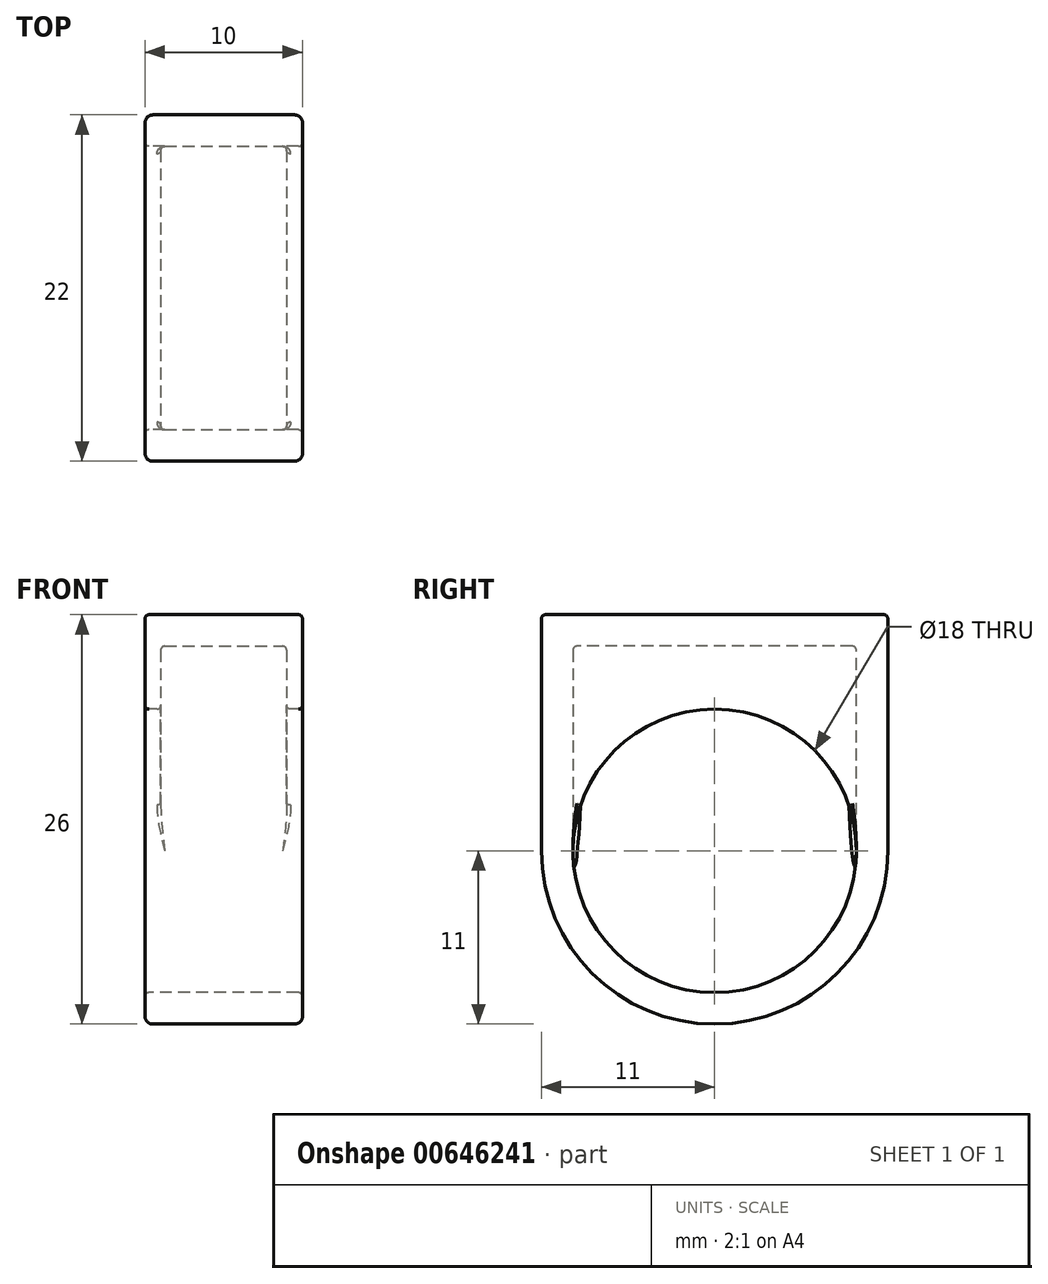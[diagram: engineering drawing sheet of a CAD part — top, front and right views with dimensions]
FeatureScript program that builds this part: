
annotation { "Feature Type Name" : "Feature", "Feature Type Description" : "" }
export const myFeature = defineFeature(function(context is Context, id is Id, definition is map)
    precondition{}
    {
        {
            var Q0;
            Q0=qCreatedBy(makeId("Right.planeOp"),FACE);
            var sketch = newSketch(context, id + "F0", { "sketchPlane" : qUnion([Q0])});
            skCircle(sketch, "E0", {"center": v(0, 0) * mm, "radius": 9 * mm});
            skCircle(sketch, "E1", {"center": v(0, 0) * mm, "radius": 11 * mm});
            skLineSegment(sketch, "E2", {"start": v(11, 0) * mm, "end": v(11, 15) * mm});
            skLineSegment(sketch, "E3", {"start": v(-11, 0) * mm, "end": v(-11, 15) * mm});
            skLineSegment(sketch, "E4", {"start": v(-11, 15) * mm, "end": v(11, 15) * mm});
            skSolve(sketch);
        }
        {
            var Q0;
            Q0=makeQuery(id+"F0.imprint","IMPRINT",FACE,{"disambiguationData":[TD([[makeQuery(id+"F0.imprint","IMPRINT",EDGE,{"derivedFrom":sQuery(id+"F0.wireOp",EDGE,"E0")}),-1.0]])]});
            var Q1;
            {var subQ0=sQuery(id+"F0.wireOp",EDGE,"E2");Q1=makeQuery(id+"F0.imprint","IMPRINT",FACE,{"disambiguationData":[TD([[makeQuery(id+"F0.imprint","IMPRINT",EDGE,{"derivedFrom":subQ0}),1.0]])]});}
            extrude(context, id + "F1", {"entities" : qUnion([Q0, Q1]), "endBound" : BoundingType.SYMMETRIC, "depth" : 10 * mm, "offsetDistance" : 25 * mm});
        }
        {
            var Q0;
            Q0=qCreatedBy(makeId("Right.planeOp"),FACE);
            var sketch = newSketch(context, id + "F2", { "sketchPlane" : qUnion([Q0])});
            skArc(sketch, "E5.0", {"start": v(-9, 0) * mm, "mid": v(0, -9) * mm, "end": v(9, 0) * mm});
            skLineSegment(sketch, "E5.1", {"start": v(-9, 13) * mm, "end": v(-9, 0) * mm});
            skLineSegment(sketch, "E5.2", {"start": v(9, 13) * mm, "end": v(-9, 13) * mm});
            skLineSegment(sketch, "E5.3", {"start": v(9, 0) * mm, "end": v(9, 13) * mm});
            skSolve(sketch);
        }
        {
            var Q0;
            Q0 = qSketchRegion(id + "F2", true);
            extrude(context, id + "F3", {"entities" : qUnion([Q0]), "operationType" : NewBodyOperationType.REMOVE, "endBound" : BoundingType.SYMMETRIC, "oppositeDirection" : true, "depth" : 8 * mm, "offsetDistance" : 25 * mm});
        }
        {
            var Q0;
            Q0=makeQuery(id+"F1.opExtrude","CAP_EDGE",EDGE,{"disambiguationData":[OSD([sQuery(id+"F0.wireOp",EDGE,"E3")])],"isStart":false});
            var Q1;
            Q1=makeQuery(id+"F1.opExtrude","CAP_EDGE",EDGE,{"disambiguationData":[OSD([sQuery(id+"F0.wireOp",EDGE,"E3")])],"isStart":true});
            fillet(context, id + "F4", {"entities" : qUnion([Q0, Q1]), "radius" : 0.5 * mm, "tangentPropagation" : true, "allowEdgeOverflow" : false});
        }
        {
            var Q0;
            Q0=makeQuery(id+"F1.opExtrude","CAP_EDGE",EDGE,{"disambiguationData":[OSD([sQuery(id+"F0.wireOp",EDGE,"E0")])],"isStart":false});
            var Q1;
            Q1=makeQuery(id+"F1.opExtrude","CAP_EDGE",EDGE,{"disambiguationData":[OSD([sQuery(id+"F0.wireOp",EDGE,"E0")])],"isStart":true});
            var Q2;
            Q2=makeQuery(id+"F1.opExtrude","SWEPT_EDGE",EDGE,{"disambiguationData":[OSD([sQuery(id+"F0.wireOp",EDGE,"E3"),sQuery(id+"F0.wireOp",EDGE,"E4")])]});
            var Q3;
            Q3=makeQuery(id+"F3.boolean.opBoolean","COPY",EDGE,{"derivedFrom":makeQuery(id+"F3.opExtrude","SWEPT_EDGE",EDGE,{"disambiguationData":[OSD([sQuery(id+"F2.wireOp",EDGE,"E5.0"),sQuery(id+"F2.wireOp",EDGE,"E5.3")])]})});
            var Q4;
            Q4=makeQuery(id+"F3.boolean.opBoolean","INTERSECT",EDGE,{"derivedFrom":[makeQuery(id+"F1.opExtrude","SWEPT_FACE",FACE,{"disambiguationData":[OSD([sQuery(id+"F0.wireOp",EDGE,"E0")])]}),makeQuery(id+"F3.opExtrude","CAP_FACE",FACE,{"disambiguationData":[OSD([sQuery(id+"F2.wireOp",EDGE,"E5.0"),sQuery(id+"F2.wireOp",EDGE,"E5.1"),sQuery(id+"F2.wireOp",EDGE,"E5.2"),sQuery(id+"F2.wireOp",EDGE,"E5.3")])],"isStart":true})]});
            var Q5;
            {var subQ0=sQuery(id+"F0.wireOp",EDGE,"E1");Q5=makeQuery(id+"F4.opFillet","BLEND_EDGE",EDGE,{"blendedFrom":[makeQuery(id+"F1.opExtrude","CAP_EDGE",EDGE,{"disambiguationData":[OSD([subQ0])],"isStart":true}),makeQuery(id+"F1.opExtrude","SWEPT_FACE",FACE,{"disambiguationData":[OSD([subQ0])]})],"blendedInto":[makeQuery(id+"F1.opExtrude","SWEPT_FACE",FACE,{"disambiguationData":[OSD([subQ0])]})]});}
            var Q6;
            Q6=makeQuery(id+"F4.opFillet","BLEND_EDGE",EDGE,{"blendedFrom":[makeQuery(id+"F1.opExtrude","CAP_EDGE",EDGE,{"disambiguationData":[OSD([sQuery(id+"F0.wireOp",EDGE,"E1")])],"isStart":false}),makeQuery(id+"F1.opExtrude","CAP_EDGE",EDGE,{"disambiguationData":[OSD([sQuery(id+"F0.wireOp",EDGE,"E3")])],"isStart":false})],"blendedInto":[]});
            var Q7;
            {var subQ0=sQuery(id+"F0.wireOp",EDGE,"E1");Q7=makeQuery(id+"F4.opFillet","BLEND_EDGE",EDGE,{"blendedFrom":[makeQuery(id+"F1.opExtrude","CAP_EDGE",EDGE,{"disambiguationData":[OSD([subQ0])],"isStart":false}),makeQuery(id+"F1.opExtrude","CAP_FACE",FACE,{"disambiguationData":[OSD([sQuery(id+"F0.wireOp",EDGE,"E0"),subQ0,sQuery(id+"F0.wireOp",EDGE,"E2"),sQuery(id+"F0.wireOp",EDGE,"E3"),sQuery(id+"F0.wireOp",EDGE,"E4")])],"isStart":false})],"blendedInto":[makeQuery(id+"F1.opExtrude","CAP_FACE",FACE,{"disambiguationData":[OSD([sQuery(id+"F0.wireOp",EDGE,"E0"),subQ0,sQuery(id+"F0.wireOp",EDGE,"E2"),sQuery(id+"F0.wireOp",EDGE,"E3"),sQuery(id+"F0.wireOp",EDGE,"E4")])],"isStart":false})]});}
            var Q8;
            {var subQ0=sQuery(id+"F0.wireOp",EDGE,"E1");Q8=makeQuery(id+"F4.opFillet","BLEND_EDGE",EDGE,{"blendedFrom":[makeQuery(id+"F1.opExtrude","CAP_EDGE",EDGE,{"disambiguationData":[OSD([subQ0])],"isStart":false}),makeQuery(id+"F1.opExtrude","SWEPT_FACE",FACE,{"disambiguationData":[OSD([subQ0])]})],"blendedInto":[makeQuery(id+"F1.opExtrude","SWEPT_FACE",FACE,{"disambiguationData":[OSD([subQ0])]})]});}
            var Q9;
            Q9=makeQuery(id+"F1.opExtrude","CAP_EDGE",EDGE,{"disambiguationData":[OSD([sQuery(id+"F0.wireOp",EDGE,"E4")])],"isStart":true});
            var Q10;
            Q10=makeQuery(id+"F1.opExtrude","CAP_EDGE",EDGE,{"disambiguationData":[OSD([sQuery(id+"F0.wireOp",EDGE,"E4")])],"isStart":false});
            var Q11;
            Q11=makeQuery(id+"F1.opExtrude","SWEPT_EDGE",EDGE,{"disambiguationData":[OSD([sQuery(id+"F0.wireOp",EDGE,"E1"),sQuery(id+"F0.wireOp",EDGE,"E2")])]});
            var Q12;
            {var subQ0=sQuery(id+"F0.wireOp",EDGE,"E2");Q12=makeQuery(id+"F4.opFillet","BLEND_EDGE",EDGE,{"blendedFrom":[makeQuery(id+"F1.opExtrude","CAP_EDGE",EDGE,{"disambiguationData":[OSD([subQ0])],"isStart":true}),makeQuery(id+"F1.opExtrude","SWEPT_FACE",FACE,{"disambiguationData":[OSD([subQ0])]})],"blendedInto":[makeQuery(id+"F1.opExtrude","SWEPT_FACE",FACE,{"disambiguationData":[OSD([subQ0])]})]});}
            var Q13;
            Q13=makeQuery(id+"F4.opFillet","BLEND_EDGE",EDGE,{"blendedFrom":[makeQuery(id+"F1.opExtrude","CAP_EDGE",EDGE,{"disambiguationData":[OSD([sQuery(id+"F0.wireOp",EDGE,"E2")])],"isStart":true}),makeQuery(id+"F1.opExtrude","SWEPT_FACE",FACE,{"disambiguationData":[OSD([sQuery(id+"F0.wireOp",EDGE,"E4")])]})],"blendedInto":[makeQuery(id+"F1.opExtrude","SWEPT_FACE",FACE,{"disambiguationData":[OSD([sQuery(id+"F0.wireOp",EDGE,"E4")])]})]});
            var Q14;
            {var subQ0=sQuery(id+"F0.wireOp",EDGE,"E2");Q14=makeQuery(id+"F4.opFillet","BLEND_EDGE",EDGE,{"blendedFrom":[makeQuery(id+"F1.opExtrude","CAP_EDGE",EDGE,{"disambiguationData":[OSD([subQ0])],"isStart":false}),makeQuery(id+"F1.opExtrude","CAP_FACE",FACE,{"disambiguationData":[OSD([sQuery(id+"F0.wireOp",EDGE,"E0"),sQuery(id+"F0.wireOp",EDGE,"E1"),subQ0,sQuery(id+"F0.wireOp",EDGE,"E3"),sQuery(id+"F0.wireOp",EDGE,"E4")])],"isStart":false})],"blendedInto":[makeQuery(id+"F1.opExtrude","CAP_FACE",FACE,{"disambiguationData":[OSD([sQuery(id+"F0.wireOp",EDGE,"E0"),sQuery(id+"F0.wireOp",EDGE,"E1"),subQ0,sQuery(id+"F0.wireOp",EDGE,"E3"),sQuery(id+"F0.wireOp",EDGE,"E4")])],"isStart":false})]});}
            var Q15;
            Q15=makeQuery(id+"F1.opExtrude","SWEPT_EDGE",EDGE,{"disambiguationData":[OSD([sQuery(id+"F0.wireOp",EDGE,"E2"),sQuery(id+"F0.wireOp",EDGE,"E4")])]});
            var Q16;
            Q16=makeQuery(id+"F1.opExtrude","SWEPT_EDGE",EDGE,{"disambiguationData":[OSD([sQuery(id+"F0.wireOp",EDGE,"E1"),sQuery(id+"F0.wireOp",EDGE,"E3")])]});
            var Q17;
            Q17=makeQuery(id+"F4.opFillet","BLEND_EDGE",EDGE,{"blendedFrom":[makeQuery(id+"F1.opExtrude","CAP_EDGE",EDGE,{"disambiguationData":[OSD([sQuery(id+"F0.wireOp",EDGE,"E1")])],"isStart":true}),makeQuery(id+"F1.opExtrude","CAP_EDGE",EDGE,{"disambiguationData":[OSD([sQuery(id+"F0.wireOp",EDGE,"E3")])],"isStart":true})],"blendedInto":[]});
            var Q18;
            {var subQ0=sQuery(id+"F0.wireOp",EDGE,"E1");Q18=makeQuery(id+"F4.opFillet","BLEND_EDGE",EDGE,{"blendedFrom":[makeQuery(id+"F1.opExtrude","CAP_EDGE",EDGE,{"disambiguationData":[OSD([subQ0])],"isStart":true}),makeQuery(id+"F1.opExtrude","CAP_FACE",FACE,{"disambiguationData":[OSD([sQuery(id+"F0.wireOp",EDGE,"E0"),subQ0,sQuery(id+"F0.wireOp",EDGE,"E2"),sQuery(id+"F0.wireOp",EDGE,"E3"),sQuery(id+"F0.wireOp",EDGE,"E4")])],"isStart":true})],"blendedInto":[makeQuery(id+"F1.opExtrude","CAP_FACE",FACE,{"disambiguationData":[OSD([sQuery(id+"F0.wireOp",EDGE,"E0"),subQ0,sQuery(id+"F0.wireOp",EDGE,"E2"),sQuery(id+"F0.wireOp",EDGE,"E3"),sQuery(id+"F0.wireOp",EDGE,"E4")])],"isStart":true})]});}
            var Q19;
            Q19=makeQuery(id+"F3.boolean.opBoolean","COPY",EDGE,{"derivedFrom":makeQuery(id+"F3.opExtrude","SWEPT_EDGE",EDGE,{"disambiguationData":[OSD([sQuery(id+"F2.wireOp",EDGE,"E5.0"),sQuery(id+"F2.wireOp",EDGE,"E5.1")])]})});
            var Q20;
            Q20=makeQuery(id+"F3.boolean.opBoolean","COPY",EDGE,{"derivedFrom":makeQuery(id+"F3.opExtrude","SWEPT_EDGE",EDGE,{"disambiguationData":[OSD([sQuery(id+"F2.wireOp",EDGE,"E5.1"),sQuery(id+"F2.wireOp",EDGE,"E5.2")])]})});
            var Q21;
            Q21=makeQuery(id+"F3.boolean.opBoolean","COPY",EDGE,{"derivedFrom":makeQuery(id+"F3.opExtrude","SWEPT_EDGE",EDGE,{"disambiguationData":[OSD([sQuery(id+"F2.wireOp",EDGE,"E5.2"),sQuery(id+"F2.wireOp",EDGE,"E5.3")])]})});
            var Q22;
            Q22=makeQuery(id+"F3.boolean.opBoolean","COPY",EDGE,{"derivedFrom":makeQuery(id+"F3.opExtrude","CAP_EDGE",EDGE,{"disambiguationData":[OSD([sQuery(id+"F2.wireOp",EDGE,"E5.2")])],"isStart":true})});
            var Q23;
            Q23=makeQuery(id+"F3.boolean.opBoolean","COPY",EDGE,{"derivedFrom":makeQuery(id+"F3.opExtrude","CAP_EDGE",EDGE,{"disambiguationData":[OSD([sQuery(id+"F2.wireOp",EDGE,"E5.2")])],"isStart":false})});
            var Q24;
            Q24=makeQuery(id+"F3.boolean.opBoolean","COPY",EDGE,{"derivedFrom":makeQuery(id+"F3.opExtrude","CAP_EDGE",EDGE,{"disambiguationData":[OSD([sQuery(id+"F2.wireOp",EDGE,"E5.3")])],"isStart":true})});
            var Q25;
            Q25=makeQuery(id+"F3.boolean.opBoolean","INTERSECT",EDGE,{"derivedFrom":[makeQuery(id+"F1.opExtrude","SWEPT_FACE",FACE,{"disambiguationData":[OSD([sQuery(id+"F0.wireOp",EDGE,"E0")])]}),makeQuery(id+"F3.opExtrude","CAP_FACE",FACE,{"disambiguationData":[OSD([sQuery(id+"F2.wireOp",EDGE,"E5.0"),sQuery(id+"F2.wireOp",EDGE,"E5.1"),sQuery(id+"F2.wireOp",EDGE,"E5.2"),sQuery(id+"F2.wireOp",EDGE,"E5.3")])],"isStart":false})]});
            var Q26;
            Q26=makeQuery(id+"F4.opFillet","BLEND_EDGE",EDGE,{"blendedFrom":[makeQuery(id+"F1.opExtrude","CAP_EDGE",EDGE,{"disambiguationData":[OSD([sQuery(id+"F0.wireOp",EDGE,"E1")])],"isStart":false}),makeQuery(id+"F1.opExtrude","CAP_EDGE",EDGE,{"disambiguationData":[OSD([sQuery(id+"F0.wireOp",EDGE,"E2")])],"isStart":false})],"blendedInto":[]});
            var Q27;
            Q27=makeQuery(id+"F4.opFillet","BLEND_EDGE",EDGE,{"blendedFrom":[makeQuery(id+"F1.opExtrude","CAP_EDGE",EDGE,{"disambiguationData":[OSD([sQuery(id+"F0.wireOp",EDGE,"E2")])],"isStart":false}),makeQuery(id+"F1.opExtrude","SWEPT_FACE",FACE,{"disambiguationData":[OSD([sQuery(id+"F0.wireOp",EDGE,"E4")])]})],"blendedInto":[makeQuery(id+"F1.opExtrude","SWEPT_FACE",FACE,{"disambiguationData":[OSD([sQuery(id+"F0.wireOp",EDGE,"E4")])]})]});
            var Q28;
            {var subQ0=sQuery(id+"F0.wireOp",EDGE,"E3");Q28=makeQuery(id+"F4.opFillet","BLEND_EDGE",EDGE,{"blendedFrom":[makeQuery(id+"F1.opExtrude","CAP_EDGE",EDGE,{"disambiguationData":[OSD([subQ0])],"isStart":true}),makeQuery(id+"F1.opExtrude","CAP_FACE",FACE,{"disambiguationData":[OSD([sQuery(id+"F0.wireOp",EDGE,"E0"),sQuery(id+"F0.wireOp",EDGE,"E1"),sQuery(id+"F0.wireOp",EDGE,"E2"),subQ0,sQuery(id+"F0.wireOp",EDGE,"E4")])],"isStart":true})],"blendedInto":[makeQuery(id+"F1.opExtrude","CAP_FACE",FACE,{"disambiguationData":[OSD([sQuery(id+"F0.wireOp",EDGE,"E0"),sQuery(id+"F0.wireOp",EDGE,"E1"),sQuery(id+"F0.wireOp",EDGE,"E2"),subQ0,sQuery(id+"F0.wireOp",EDGE,"E4")])],"isStart":true})]});}
            var Q29;
            {var subQ0=sQuery(id+"F0.wireOp",EDGE,"E3");Q29=makeQuery(id+"F4.opFillet","BLEND_EDGE",EDGE,{"blendedFrom":[makeQuery(id+"F1.opExtrude","CAP_EDGE",EDGE,{"disambiguationData":[OSD([subQ0])],"isStart":true}),makeQuery(id+"F1.opExtrude","SWEPT_FACE",FACE,{"disambiguationData":[OSD([subQ0])]})],"blendedInto":[makeQuery(id+"F1.opExtrude","SWEPT_FACE",FACE,{"disambiguationData":[OSD([subQ0])]})]});}
            var Q30;
            Q30=makeQuery(id+"F4.opFillet","BLEND_EDGE",EDGE,{"blendedFrom":[makeQuery(id+"F1.opExtrude","CAP_EDGE",EDGE,{"disambiguationData":[OSD([sQuery(id+"F0.wireOp",EDGE,"E3")])],"isStart":true}),makeQuery(id+"F1.opExtrude","SWEPT_FACE",FACE,{"disambiguationData":[OSD([sQuery(id+"F0.wireOp",EDGE,"E4")])]})],"blendedInto":[makeQuery(id+"F1.opExtrude","SWEPT_FACE",FACE,{"disambiguationData":[OSD([sQuery(id+"F0.wireOp",EDGE,"E4")])]})]});
            var Q31;
            {var subQ0=sQuery(id+"F0.wireOp",EDGE,"E3");Q31=makeQuery(id+"F4.opFillet","BLEND_EDGE",EDGE,{"blendedFrom":[makeQuery(id+"F1.opExtrude","CAP_EDGE",EDGE,{"disambiguationData":[OSD([subQ0])],"isStart":false}),makeQuery(id+"F1.opExtrude","CAP_FACE",FACE,{"disambiguationData":[OSD([sQuery(id+"F0.wireOp",EDGE,"E0"),sQuery(id+"F0.wireOp",EDGE,"E1"),sQuery(id+"F0.wireOp",EDGE,"E2"),subQ0,sQuery(id+"F0.wireOp",EDGE,"E4")])],"isStart":false})],"blendedInto":[makeQuery(id+"F1.opExtrude","CAP_FACE",FACE,{"disambiguationData":[OSD([sQuery(id+"F0.wireOp",EDGE,"E0"),sQuery(id+"F0.wireOp",EDGE,"E1"),sQuery(id+"F0.wireOp",EDGE,"E2"),subQ0,sQuery(id+"F0.wireOp",EDGE,"E4")])],"isStart":false})]});}
            var Q32;
            {var subQ0=sQuery(id+"F0.wireOp",EDGE,"E3");Q32=makeQuery(id+"F4.opFillet","BLEND_EDGE",EDGE,{"blendedFrom":[makeQuery(id+"F1.opExtrude","CAP_EDGE",EDGE,{"disambiguationData":[OSD([subQ0])],"isStart":false}),makeQuery(id+"F1.opExtrude","SWEPT_FACE",FACE,{"disambiguationData":[OSD([subQ0])]})],"blendedInto":[makeQuery(id+"F1.opExtrude","SWEPT_FACE",FACE,{"disambiguationData":[OSD([subQ0])]})]});}
            var Q33;
            Q33=makeQuery(id+"F4.opFillet","BLEND_EDGE",EDGE,{"blendedFrom":[makeQuery(id+"F1.opExtrude","CAP_EDGE",EDGE,{"disambiguationData":[OSD([sQuery(id+"F0.wireOp",EDGE,"E3")])],"isStart":false}),makeQuery(id+"F1.opExtrude","SWEPT_FACE",FACE,{"disambiguationData":[OSD([sQuery(id+"F0.wireOp",EDGE,"E4")])]})],"blendedInto":[makeQuery(id+"F1.opExtrude","SWEPT_FACE",FACE,{"disambiguationData":[OSD([sQuery(id+"F0.wireOp",EDGE,"E4")])]})]});
            var Q34;
            Q34=makeQuery(id+"F4.opFillet","BLEND_EDGE",EDGE,{"blendedFrom":[makeQuery(id+"F1.opExtrude","CAP_EDGE",EDGE,{"disambiguationData":[OSD([sQuery(id+"F0.wireOp",EDGE,"E1")])],"isStart":true}),makeQuery(id+"F1.opExtrude","CAP_EDGE",EDGE,{"disambiguationData":[OSD([sQuery(id+"F0.wireOp",EDGE,"E2")])],"isStart":true})],"blendedInto":[]});
            var Q35;
            Q35=makeQuery(id+"F3.boolean.opBoolean","COPY",EDGE,{"derivedFrom":makeQuery(id+"F3.opExtrude","CAP_EDGE",EDGE,{"disambiguationData":[OSD([sQuery(id+"F2.wireOp",EDGE,"E5.1")])],"isStart":true})});
            var Q36;
            Q36=makeQuery(id+"F3.boolean.opBoolean","COPY",EDGE,{"derivedFrom":makeQuery(id+"F3.opExtrude","CAP_EDGE",EDGE,{"disambiguationData":[OSD([sQuery(id+"F2.wireOp",EDGE,"E5.1")])],"isStart":false})});
            var Q37;
            Q37=makeQuery(id+"F3.boolean.opBoolean","COPY",EDGE,{"derivedFrom":makeQuery(id+"F3.opExtrude","CAP_EDGE",EDGE,{"disambiguationData":[OSD([sQuery(id+"F2.wireOp",EDGE,"E5.3")])],"isStart":false})});
            var Q38;
            {var subQ0=sQuery(id+"F0.wireOp",EDGE,"E2");Q38=makeQuery(id+"F4.opFillet","BLEND_EDGE",EDGE,{"blendedFrom":[makeQuery(id+"F1.opExtrude","CAP_EDGE",EDGE,{"disambiguationData":[OSD([subQ0])],"isStart":true}),makeQuery(id+"F1.opExtrude","CAP_FACE",FACE,{"disambiguationData":[OSD([sQuery(id+"F0.wireOp",EDGE,"E0"),sQuery(id+"F0.wireOp",EDGE,"E1"),subQ0,sQuery(id+"F0.wireOp",EDGE,"E3"),sQuery(id+"F0.wireOp",EDGE,"E4")])],"isStart":true})],"blendedInto":[makeQuery(id+"F1.opExtrude","CAP_FACE",FACE,{"disambiguationData":[OSD([sQuery(id+"F0.wireOp",EDGE,"E0"),sQuery(id+"F0.wireOp",EDGE,"E1"),subQ0,sQuery(id+"F0.wireOp",EDGE,"E3"),sQuery(id+"F0.wireOp",EDGE,"E4")])],"isStart":true})]});}
            var Q39;
            {var subQ0=sQuery(id+"F0.wireOp",EDGE,"E2");Q39=makeQuery(id+"F4.opFillet","BLEND_EDGE",EDGE,{"blendedFrom":[makeQuery(id+"F1.opExtrude","CAP_EDGE",EDGE,{"disambiguationData":[OSD([subQ0])],"isStart":false}),makeQuery(id+"F1.opExtrude","SWEPT_FACE",FACE,{"disambiguationData":[OSD([subQ0])]})],"blendedInto":[makeQuery(id+"F1.opExtrude","SWEPT_FACE",FACE,{"disambiguationData":[OSD([subQ0])]})]});}
            fillet(context, id + "F5", {"entities" : qUnion([Q0, Q1, Q2, Q3, Q4, Q5, Q6, Q7, Q8, Q9, Q10, Q11, Q12, Q13, Q14, Q15, Q16, Q17, Q18, Q19, Q20, Q21, Q22, Q23, Q24, Q25, Q26, Q27, Q28, Q29, Q30, Q31, Q32, Q33, Q34, Q35, Q36, Q37, Q38, Q39]), "radius" : 0.25 * mm, "tangentPropagation" : true, "allowEdgeOverflow" : false});
        }
    });
